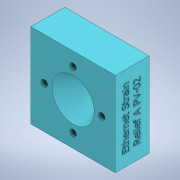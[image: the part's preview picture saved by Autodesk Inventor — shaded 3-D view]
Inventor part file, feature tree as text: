
AUTODESK INVENTOR PART (.ipt)
format: ipt  version: 2022.2 (Build 262287000, 287)  size: 1,226,752 bytes
history: native  units: mm
features: sketch x7, extrude x2, revolve x2, emboss x2, hole x1, plane x1
ambient origin geometry x8: Origin, YZ Plane, XZ Plane, XY Plane, X Axis, Y Axis, Z Axis, Center Point
bodies: Solid7 (feature_tree)
feature tree (15):
  extrude  "Extrusion20"  Depth=50.0mm
  revolve  "Revolution4"  [1 undecoded]
  extrude  "Extrusion21"  TaperAngle=90.0deg  [1 undecoded]
  revolve  "Revolution5"  [1 undecoded]
  hole  "Hole2"  [1 undecoded]
  plane  "Work Plane6"
  emboss  "Emboss3"
  emboss  "Emboss4"
  sketch  "Sketch27"  dims[d124=50.0mm d125=50.0mm]
  sketch  "Sketch28"  dims[d126=15.0mm d127=0.0mm d128=3.0mm]
  sketch  "Sketch29"  dims[d129=12.5mm d130=90.0deg]
  sketch  "Sketch30"  dims[d131=5.0mm d132=0.0mm d133=2.5mm]
  sketch  "Sketch31"  dims[d134=90.0deg d135=34.0mm]
  sketch  "Sketch32"  dims[d136=34.0mm]
  sketch  "Sketch33"  dims[d137=3.81mm d138=6.0mm d139=8.89mm d140=3.145mm d141=14.3117mm d142=8.0mm d143=20.594885mm d144=1.0mm d145=0.0mm d146=1.0mm d147=0.0mm]
note: 4 required parameter values undecoded (feature->parameter linkage not recoverable at this tier; creation-order binding heuristic only, values carry confidence <= 0.55)